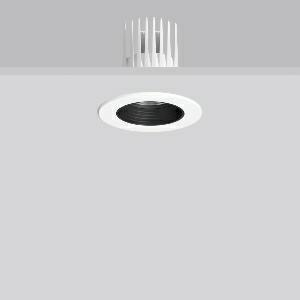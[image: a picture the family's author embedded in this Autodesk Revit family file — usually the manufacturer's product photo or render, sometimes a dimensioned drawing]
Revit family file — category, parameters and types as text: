
# Revit family: heledon_mini_e_901746_002_2_76_86ca
name_source: partatom
category: Lighting Fixtures
units: mm (PartAtom-declared; Revit-internal decimal feet)

## family parameters
Cut with Voids When Loaded = No
Host = Face
Light Source = No
Part Type = Normal
Room Calculation Point = No
Round Connector Dimension = Use Diameter
Shared = No

## types (1)
- HELEDON mini E (1 x LED Modul 927, 2150 lm, 2700)
    Apparent Load = 20 VA
    Approval mark = CE
    CIE Flux Codes = 80 99 100 100 100
    Color Rendering = 92
    Color Temperature = 2700
    Default Elevation = 1800 mm
    Description = Series: HELEDON mini
Round recessed downlight. Housing: die-cast aluminium, powder-coated. Black plastic ring and recessed LED to prevent glare from the side. Optical assembly with lens made of plastic (polycarbonate) for the best homogeneous light distribution - can be changed without tools. Best colour rendering index Ra>90. Suitable for Recessed ceiling mounting. Installation without tools thanks to spring fastening system. Including separate LED converter with connecting cable 600 mm.High quality converter without flickering and stroboscopic effect. Through-wiring box (5 pole) available as accessory. The following accessories can be mounted without use of tools: interchangeable lenses, decorative glasses, honeycomb louvre, clear and frosted diffusers, white interchangeable plastic ring. 
Colour: traffic white, matt (RAL 9016)
Diameter: 124 mm
Height: 3 mm
Cut-out diameter: 114 mm
Recess height: 170 mm
Luminaire: recess height: 120 mm
Lamp: LED
Socket: without socket
Colour temperature: 2700K
Colour rendering index (CRI): 92
System power: 20 W
Rated luminous flux: 2150 lm
Luminous efficiency: 108 lm/W
Control gear: Converter, dimmable, DALI
Protection class: II
Type of protection: IP 20
    Height = 0 mm  [stored 0 ft]
    Lamp = 1 x LED Modul 927
    Lamp Light Flux = 2150 lm
    Lamp count = 1
    Length = 124 mm  [stored 0.406824 ft]
    Lifetime = 50000 h
    Luminous efficacy = 108 lm/W
    Manufacturer = RZB
    ModVariant = No
    Model = 901746.002.2.76
    Mounting Place = Ceiling
    Mounting Type = Recessed
    Number of Poles = 1
    OnlyDefault = Yes
    Power Factor = 1
    Product Name = HELEDON mini E
    Product group = Recessed downlights
    ProductGroupID = 402
    Protection Class = Protection class II
    Protection Degree = IP 20
    RLX_Detail_Level = 1
    RLX_Emergency_Light_Flux = 0 lm
    RLX_Emergency_Type = 0
    RLX_Emergency_Type_DB = No
    RlxData = <blob elided: 126861 chars, md5=b6256ee8>
    Socket = socket
    Standby Power = 0 W
    System Light Flux = 2150 lm
    System Power = 20 W
    Type Comments = Product without accessories
    Type Image = 901656.002.jpg
    URL = http://relux.com
    VarID = ---
    Voltage = 230 V
    Voltage Range = 220-240 V
    Weight = 0.00 kg
    Width = 0 mm  [stored 0 ft]

note: [stored X ft] marks values corroborated as IEEE doubles in the binary element streams (Revit-internal decimal feet)

## geometry (parser evidence)
native form markers: Blend x4, Sweep x12
no freeform markers — native parametric forms only
